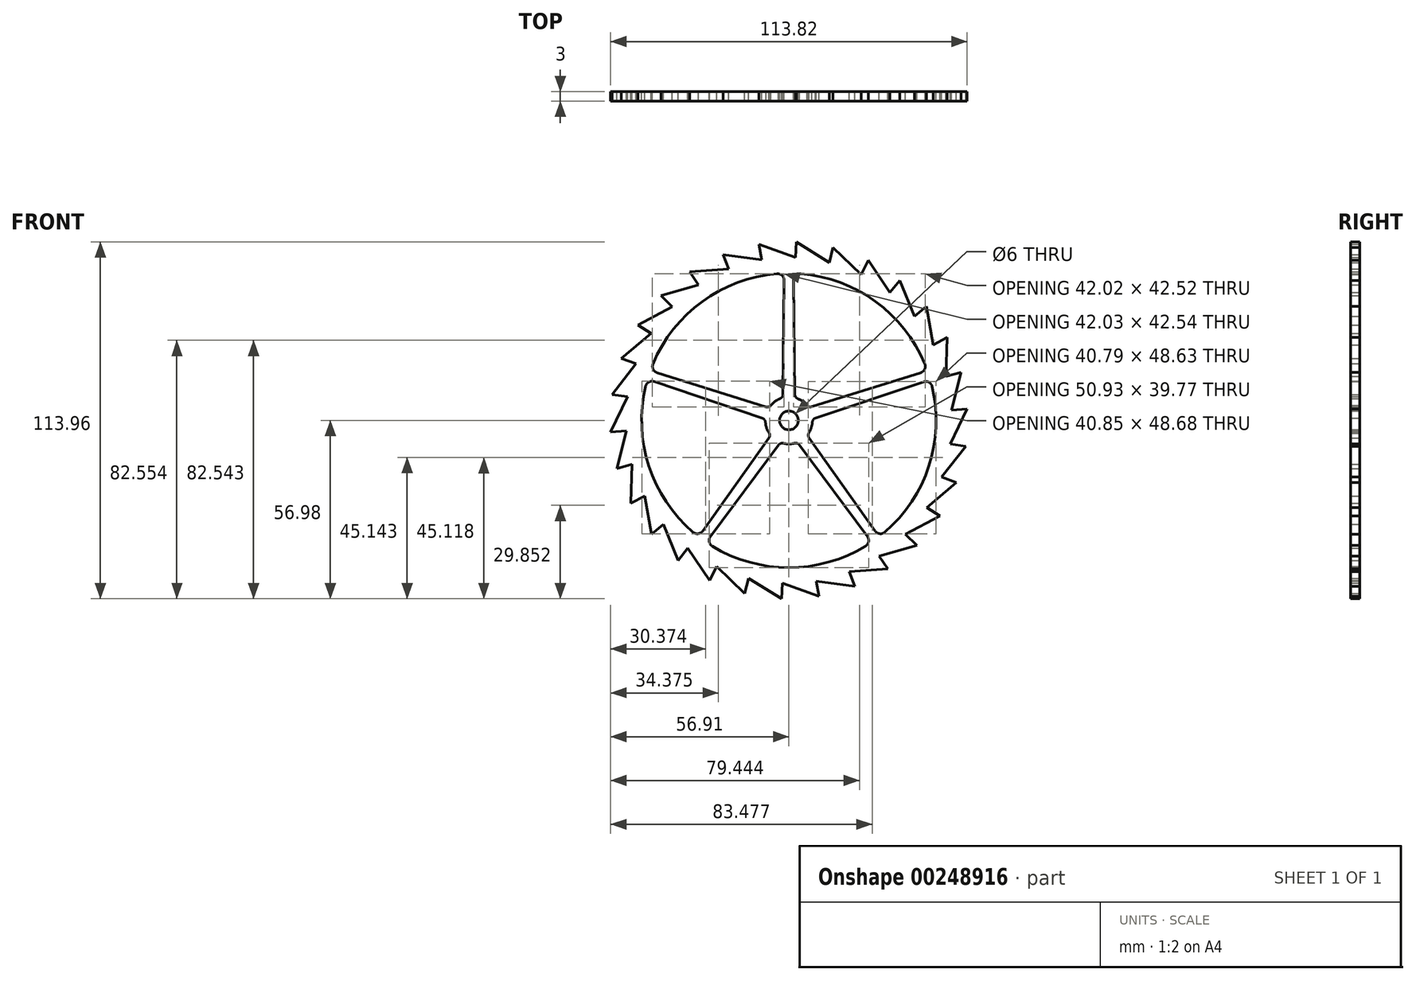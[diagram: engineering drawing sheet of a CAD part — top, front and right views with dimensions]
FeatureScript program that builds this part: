
annotation { "Feature Type Name" : "Feature", "Feature Type Description" : "" }
export const myFeature = defineFeature(function(context is Context, id is Id, definition is map)
    precondition{}
    {
        {
            var Q0;
            Q0=qCreatedBy(makeId("Front.planeOp"),FACE);
            var sketch = newSketch(context, id + "F0", { "sketchPlane" : qUnion([Q0])});
            skLineSegment(sketch, "E0", {"start": v(16.93, -54.43) * mm, "end": v(16.97, -54.42) * mm});
            skCircle(sketch, "E1", {"center": v(-0.03, 0) * mm, "radius": 52 * mm});
            skLineSegment(sketch, "E2.10.0", {"start": v(-40.04, -33.2) * mm, "end": v(-43.9, -36.4) * mm});
            skLineSegment(sketch, "E2.10.1", {"start": v(-43.9, -36.4) * mm, "end": v(-46.08, -24.16) * mm});
            skPoint(sketch, "E3.visualSharp", {"position": v(33.26, -42.81) * mm});
            skArc(sketch, "E3.filletArc", {"start": v(33.31, -42.89) * mm, "mid": v(33.25, -42.83) * mm, "end": v(33.17, -42.8) * mm});
            skArc(sketch, "E4", {"start": v(35.3, 44.72) * mm, "mid": v(35.3, 44.73) * mm, "end": v(35.3, 44.73) * mm});
            skLineSegment(sketch, "E5", {"start": v(32.2, 40.8) * mm, "end": v(32.2, 40.82) * mm});
            skLineSegment(sketch, "E6", {"start": v(0, 52) * mm, "end": v(0, 52.7) * mm, "construction": true});
            skPoint(sketch, "E7.orphan", {"position": v(0, 4.97) * mm});
            skArc(sketch, "E8", {"start": v(-45.72, 10.9) * mm, "mid": v(-44.7, -14.51) * mm, "end": v(-30.6, -35.68) * mm});
            skArc(sketch, "E9", {"start": v(5.77, 4.78) * mm, "mid": v(4.43, 6.04) * mm, "end": v(2.81, 6.94) * mm});
            skLineSegment(sketch, "E10", {"start": v(0, -0.01) * mm, "end": v(0, 64.97) * mm, "construction": true});
            skLineSegment(sketch, "E11", {"start": v(-1.52, 44.7) * mm, "end": v(-1.9, 8.35) * mm});
            skLineSegment(sketch, "E12.MirrorCS", {"start": v(1.52, 44.84) * mm, "end": v(1.9, 8.29) * mm});
            skLineSegment(sketch, "E13.1.0", {"start": v(-44.26, 15.93) * mm, "end": v(-44.22, 15.92) * mm});
            skLineSegment(sketch, "E13.1.1", {"start": v(-45.2, 13.14) * mm, "end": v(-45.13, 13.12) * mm});
            skLineSegment(sketch, "E13.2.0", {"start": v(-28.85, -37.17) * mm, "end": v(-28.83, -37.13) * mm});
            skLineSegment(sketch, "E13.2.1", {"start": v(-26.43, -38.93) * mm, "end": v(-26.4, -38.9) * mm});
            skLineSegment(sketch, "E14.2.3.0", {"start": v(26.43, -38.94) * mm, "end": v(26.4, -38.9) * mm});
            skLineSegment(sketch, "E14.3.3.0", {"start": v(28.86, -37.19) * mm, "end": v(28.82, -37.13) * mm});
            skLineSegment(sketch, "E14.2.4.0", {"start": v(45.18, 13.08) * mm, "end": v(45.14, 13.07) * mm});
            skLineSegment(sketch, "E14.3.4.0", {"start": v(42.07, 15.25) * mm, "end": v(7.32, 4.38) * mm});
            skLineSegment(sketch, "E15.trimOffspring", {"start": v(-7.5, 0) * mm, "end": v(-64.05, 0) * mm, "construction": true});
            skArc(sketch, "E16.trimOffspring", {"start": v(-2.87, 6.92) * mm, "mid": v(-4.45, 6.03) * mm, "end": v(-5.77, 4.78) * mm});
            skArc(sketch, "E17.trimOffspring", {"start": v(-7.48, -0.6) * mm, "mid": v(-7.1, -2.42) * mm, "end": v(-6.3, -4.09) * mm});
            skArc(sketch, "E18.trimOffspring", {"start": v(-1.74, -7.3) * mm, "mid": v(0.1, -7.51) * mm, "end": v(1.93, -7.26) * mm});
            skArc(sketch, "E19.trimOffspring", {"start": v(6.33, -4.03) * mm, "mid": v(7.12, -2.37) * mm, "end": v(7.48, -0.58) * mm});
            skArc(sketch, "E20.trimOffspring", {"start": v(43.38, 18.07) * mm, "mid": v(27.62, 38.02) * mm, "end": v(3.77, 46.84) * mm});
            skArc(sketch, "E21.trimOffspring", {"start": v(-3.82, 46.83) * mm, "mid": v(-27.64, 38) * mm, "end": v(-43.39, 18.06) * mm});
            skArc(sketch, "E22.trimOffspring", {"start": v(-24.44, -40.15) * mm, "mid": v(0, -47.01) * mm, "end": v(24.44, -40.15) * mm});
            skArc(sketch, "E23.trimOffspring", {"start": v(30.6, -35.68) * mm, "mid": v(44.7, -14.54) * mm, "end": v(45.73, 10.85) * mm});
            skArc(sketch, "E24", {"start": v(-30.6, -35.68) * mm, "mid": v(-28.98, -36.17) * mm, "end": v(-27.52, -35.3) * mm});
            skArc(sketch, "E25.MirrorC", {"start": v(-24.44, -40.15) * mm, "mid": v(-25.42, -38.75) * mm, "end": v(-25.04, -37.07) * mm});
            skArc(sketch, "E26.MirrorC", {"start": v(24.44, -40.15) * mm, "mid": v(25.42, -38.75) * mm, "end": v(25.05, -37.08) * mm});
            skArc(sketch, "E27.MirrorC", {"start": v(30.6, -35.68) * mm, "mid": v(28.98, -36.17) * mm, "end": v(27.52, -35.3) * mm});
            skArc(sketch, "E28.MirrorC", {"start": v(45.73, 10.85) * mm, "mid": v(44.7, 12.2) * mm, "end": v(43.01, 12.35) * mm});
            skArc(sketch, "E29.MirrorC", {"start": v(43.38, 18.07) * mm, "mid": v(43.35, 16.37) * mm, "end": v(42.07, 15.25) * mm});
            skPoint(sketch, "E30.endSnap0", {"position": v(22.9, 31.47) * mm});
            skArc(sketch, "E31.MirrorC", {"start": v(3.81, 46.83) * mm, "mid": v(2.15, 46.24) * mm, "end": v(1.52, 44.6) * mm});
            skArc(sketch, "E32.MirrorC", {"start": v(-3.82, 46.83) * mm, "mid": v(-2.2, 46.27) * mm, "end": v(-1.52, 44.7) * mm});
            skArc(sketch, "E33.MirrorC", {"start": v(-43.39, 18.06) * mm, "mid": v(-43.35, 16.36) * mm, "end": v(-42.07, 15.24) * mm});
            skArc(sketch, "E34.MirrorC", {"start": v(-45.72, 10.9) * mm, "mid": v(-44.69, 12.25) * mm, "end": v(-43, 12.4) * mm});
            skPoint(sketch, "E35.orphan", {"position": v(1.5, 47.02) * mm});
            skPoint(sketch, "E36.orphan", {"position": v(-1.5, 47.02) * mm});
            skLineSegment(sketch, "E37.trimOffspring", {"start": v(43.01, 12.35) * mm, "end": v(8.5, 0.77) * mm});
            skLineSegment(sketch, "E38.trimOffspring", {"start": v(27.52, -35.3) * mm, "end": v(6.45, -5.62) * mm});
            skLineSegment(sketch, "E39.trimOffspring", {"start": v(25.05, -37.08) * mm, "end": v(3.36, -7.84) * mm});
            skLineSegment(sketch, "E40.trimOffspring", {"start": v(-25.04, -37.07) * mm, "end": v(-3.31, -7.84) * mm});
            skLineSegment(sketch, "E41.trimOffspring", {"start": v(-27.52, -35.3) * mm, "end": v(-6.42, -5.65) * mm});
            skLineSegment(sketch, "E42.trimOffspring", {"start": v(-42.07, 15.24) * mm, "end": v(-7.33, 4.35) * mm});
            skLineSegment(sketch, "E43.trimOffspring", {"start": v(-43, 12.4) * mm, "end": v(-8.54, 0.75) * mm});
            skArc(sketch, "E44", {"start": v(-7.48, -0.6) * mm, "mid": v(-7.8, 0.23) * mm, "end": v(-8.54, 0.75) * mm});
            skArc(sketch, "E45.MirrorCS", {"start": v(2.81, 6.94) * mm, "mid": v(2.17, 7.49) * mm, "end": v(1.9, 8.29) * mm});
            skArc(sketch, "E46.MirrorCS", {"start": v(-1.74, -7.3) * mm, "mid": v(-2.6, -7.35) * mm, "end": v(-3.31, -7.84) * mm});
            skArc(sketch, "E47.MirrorCS", {"start": v(-5.77, 4.78) * mm, "mid": v(-6.49, 4.35) * mm, "end": v(-7.33, 4.35) * mm});
            skArc(sketch, "E48.MirrorCS", {"start": v(-2.87, 6.92) * mm, "mid": v(-2.17, 7.49) * mm, "end": v(-1.9, 8.35) * mm});
            skArc(sketch, "E49.MirrorCS", {"start": v(5.77, 4.78) * mm, "mid": v(6.5, 4.36) * mm, "end": v(7.32, 4.38) * mm});
            skArc(sketch, "E50.MirrorCS", {"start": v(7.48, -0.58) * mm, "mid": v(7.8, 0.24) * mm, "end": v(8.5, 0.77) * mm});
            skArc(sketch, "E51.MirrorCS", {"start": v(6.33, -4.03) * mm, "mid": v(6.17, -4.84) * mm, "end": v(6.45, -5.62) * mm});
            skArc(sketch, "E52.MirrorCS", {"start": v(1.93, -7.26) * mm, "mid": v(2.72, -7.36) * mm, "end": v(3.36, -7.84) * mm});
            skArc(sketch, "E53.trimOffspring", {"start": v(-6.3, -4.09) * mm, "mid": v(-6.11, -4.89) * mm, "end": v(-6.42, -5.65) * mm});
            skCircle(sketch, "E54", {"center": v(0, 0) * mm, "radius": 3 * mm});
            skCircle(sketch, "E55", {"center": v(0, 0) * mm, "radius": 7.32 * mm, "construction": true});
            skLineSegment(sketch, "E56", {"start": v(0, 0) * mm, "end": v(-46.08, -24.16) * mm, "construction": true});
            skLineSegment(sketch, "E57", {"start": v(0, 0) * mm, "end": v(-40.04, -33.2) * mm, "construction": true});
            skLineSegment(sketch, "E58.1.0", {"start": v(-35.36, -44.73) * mm, "end": v(-40.05, -33.21) * mm});
            skLineSegment(sketch, "E58.1.1", {"start": v(-32.26, -40.8) * mm, "end": v(-35.36, -44.73) * mm});
            skLineSegment(sketch, "E58.2.0", {"start": v(-25.3, -51.1) * mm, "end": v(-32.27, -40.81) * mm});
            skLineSegment(sketch, "E58.2.1", {"start": v(-23.08, -46.63) * mm, "end": v(-25.3, -51.1) * mm});
            skLineSegment(sketch, "E58.3.0", {"start": v(-14.11, -55.25) * mm, "end": v(-23.08, -46.63) * mm});
            skLineSegment(sketch, "E58.3.1", {"start": v(-12.88, -50.4) * mm, "end": v(-14.11, -55.25) * mm});
            skLineSegment(sketch, "E58.4.0", {"start": v(-2.32, -56.98) * mm, "end": v(-12.88, -50.4) * mm});
            skLineSegment(sketch, "E58.4.1", {"start": v(-2.12, -51.98) * mm, "end": v(-2.32, -56.98) * mm});
            skLineSegment(sketch, "E58.5.0", {"start": v(9.58, -56.21) * mm, "end": v(-2.12, -51.98) * mm});
            skLineSegment(sketch, "E58.5.1", {"start": v(8.74, -51.28) * mm, "end": v(9.58, -56.21) * mm});
            skLineSegment(sketch, "E58.6.0", {"start": v(21.06, -53) * mm, "end": v(8.74, -51.29) * mm});
            skLineSegment(sketch, "E58.6.1", {"start": v(19.2, -48.35) * mm, "end": v(21.06, -53) * mm});
            skLineSegment(sketch, "E58.7.0", {"start": v(31.61, -47.46) * mm, "end": v(19.21, -48.35) * mm});
            skLineSegment(sketch, "E58.7.1", {"start": v(28.84, -43.3) * mm, "end": v(31.61, -47.46) * mm});
            skLineSegment(sketch, "E58.8.0", {"start": v(40.8, -39.85) * mm, "end": v(28.84, -43.3) * mm});
            skLineSegment(sketch, "E58.8.1", {"start": v(37.21, -36.35) * mm, "end": v(40.8, -39.85) * mm});
            skLineSegment(sketch, "E58.9.0", {"start": v(48.18, -30.5) * mm, "end": v(37.22, -36.36) * mm});
            skLineSegment(sketch, "E58.9.1", {"start": v(43.96, -27.82) * mm, "end": v(48.18, -30.5) * mm});
            skLineSegment(sketch, "E58.10.0", {"start": v(53.47, -19.81) * mm, "end": v(43.96, -27.82) * mm});
            skLineSegment(sketch, "E58.10.1", {"start": v(48.78, -18.08) * mm, "end": v(53.47, -19.81) * mm});
            skLineSegment(sketch, "E58.11.0", {"start": v(56.42, -8.26) * mm, "end": v(48.79, -18.08) * mm});
            skLineSegment(sketch, "E58.11.1", {"start": v(51.47, -7.54) * mm, "end": v(56.42, -8.26) * mm});
            skLineSegment(sketch, "E58.12.0", {"start": v(56.9, 3.65) * mm, "end": v(51.48, -7.54) * mm});
            skLineSegment(sketch, "E58.12.1", {"start": v(51.92, 3.33) * mm, "end": v(56.9, 3.65) * mm});
            skLineSegment(sketch, "E58.13.0", {"start": v(54.9, 15.4) * mm, "end": v(51.92, 3.33) * mm});
            skLineSegment(sketch, "E58.13.1", {"start": v(50.09, 14.05) * mm, "end": v(54.9, 15.4) * mm});
            skLineSegment(sketch, "E58.14.0", {"start": v(50.5, 26.48) * mm, "end": v(50.1, 14.05) * mm});
            skLineSegment(sketch, "E58.14.1", {"start": v(46.07, 24.16) * mm, "end": v(50.5, 26.48) * mm});
            skLineSegment(sketch, "E58.15.0", {"start": v(43.9, 36.4) * mm, "end": v(46.08, 24.16) * mm});
            skLineSegment(sketch, "E58.15.1", {"start": v(40.04, 33.2) * mm, "end": v(43.9, 36.4) * mm});
            skLineSegment(sketch, "E58.16.0", {"start": v(35.36, 44.73) * mm, "end": v(40.05, 33.21) * mm});
            skLineSegment(sketch, "E58.16.1", {"start": v(32.26, 40.8) * mm, "end": v(35.36, 44.73) * mm});
            skLineSegment(sketch, "E58.17.0", {"start": v(25.3, 51.1) * mm, "end": v(32.27, 40.81) * mm});
            skLineSegment(sketch, "E58.17.1", {"start": v(23.08, 46.63) * mm, "end": v(25.3, 51.1) * mm});
            skLineSegment(sketch, "E58.18.0", {"start": v(14.11, 55.25) * mm, "end": v(23.08, 46.63) * mm});
            skLineSegment(sketch, "E58.18.1", {"start": v(12.88, 50.4) * mm, "end": v(14.11, 55.25) * mm});
            skLineSegment(sketch, "E58.19.0", {"start": v(2.32, 56.98) * mm, "end": v(12.88, 50.4) * mm});
            skLineSegment(sketch, "E58.19.1", {"start": v(2.12, 51.98) * mm, "end": v(2.32, 56.98) * mm});
            skLineSegment(sketch, "E58.20.0", {"start": v(-9.58, 56.21) * mm, "end": v(2.12, 51.98) * mm});
            skLineSegment(sketch, "E58.20.1", {"start": v(-8.74, 51.28) * mm, "end": v(-9.58, 56.21) * mm});
            skLineSegment(sketch, "E58.21.0", {"start": v(-21.06, 53) * mm, "end": v(-8.74, 51.29) * mm});
            skLineSegment(sketch, "E58.21.1", {"start": v(-19.2, 48.35) * mm, "end": v(-21.06, 53) * mm});
            skLineSegment(sketch, "E58.22.0", {"start": v(-31.61, 47.46) * mm, "end": v(-19.21, 48.35) * mm});
            skLineSegment(sketch, "E58.22.1", {"start": v(-28.84, 43.3) * mm, "end": v(-31.61, 47.46) * mm});
            skLineSegment(sketch, "E58.23.0", {"start": v(-40.8, 39.85) * mm, "end": v(-28.84, 43.3) * mm});
            skLineSegment(sketch, "E58.23.1", {"start": v(-37.21, 36.35) * mm, "end": v(-40.8, 39.85) * mm});
            skLineSegment(sketch, "E58.24.0", {"start": v(-48.18, 30.5) * mm, "end": v(-37.22, 36.36) * mm});
            skLineSegment(sketch, "E58.24.1", {"start": v(-43.96, 27.82) * mm, "end": v(-48.18, 30.5) * mm});
            skLineSegment(sketch, "E58.25.0", {"start": v(-53.47, 19.81) * mm, "end": v(-43.96, 27.82) * mm});
            skLineSegment(sketch, "E58.25.1", {"start": v(-48.78, 18.08) * mm, "end": v(-53.47, 19.81) * mm});
            skLineSegment(sketch, "E58.26.0", {"start": v(-56.42, 8.26) * mm, "end": v(-48.79, 18.08) * mm});
            skLineSegment(sketch, "E58.26.1", {"start": v(-51.47, 7.54) * mm, "end": v(-56.42, 8.26) * mm});
            skLineSegment(sketch, "E58.27.0", {"start": v(-56.9, -3.65) * mm, "end": v(-51.48, 7.54) * mm});
            skLineSegment(sketch, "E58.27.1", {"start": v(-51.92, -3.33) * mm, "end": v(-56.9, -3.65) * mm});
            skLineSegment(sketch, "E58.28.0", {"start": v(-54.9, -15.4) * mm, "end": v(-51.92, -3.33) * mm});
            skLineSegment(sketch, "E58.28.1", {"start": v(-50.09, -14.05) * mm, "end": v(-54.9, -15.4) * mm});
            skLineSegment(sketch, "E58.29.0", {"start": v(-50.5, -26.48) * mm, "end": v(-50.1, -14.05) * mm});
            skLineSegment(sketch, "E58.29.1", {"start": v(-46.07, -24.16) * mm, "end": v(-50.5, -26.48) * mm});
            skSolve(sketch);
        }
        {
            var Q0;
            {var subQ0=sQuery(id+"F0.wireOp",EDGE,"E58.28.0");var subQ1=sQuery(id+"F0.wireOp",EDGE,"E1");var subQ2=makeQuery(id+"F0.imprint","INTERSECT",VERTEX,{"derivedFrom":[subQ1,subQ0]});Q0=makeQuery(id+"F0.imprint","IMPRINT",FACE,{"disambiguationData":[TD([[makeQuery(id+"F0.imprint","IMPRINT",EDGE,{"disambiguationData":[TD([[subQ2,-1.0]])],"derivedFrom":subQ1}),-1.0]])]});}
            var Q1;
            {var subQ0=sQuery(id+"F0.wireOp",EDGE,"E58.29.0");var subQ1=sQuery(id+"F0.wireOp",EDGE,"E1");var subQ2=makeQuery(id+"F0.imprint","INTERSECT",VERTEX,{"derivedFrom":[subQ1,subQ0]});Q1=makeQuery(id+"F0.imprint","IMPRINT",FACE,{"disambiguationData":[TD([[makeQuery(id+"F0.imprint","IMPRINT",EDGE,{"disambiguationData":[TD([[subQ2,-1.0]])],"derivedFrom":subQ1}),-1.0]])]});}
            var Q2;
            {var subQ0=sQuery(id+"F0.wireOp",EDGE,"E2.10.1");var subQ1=sQuery(id+"F0.wireOp",EDGE,"E1");var subQ2=makeQuery(id+"F0.imprint","INTERSECT",VERTEX,{"derivedFrom":[subQ1,subQ0]});Q2=makeQuery(id+"F0.imprint","IMPRINT",FACE,{"disambiguationData":[TD([[makeQuery(id+"F0.imprint","IMPRINT",EDGE,{"disambiguationData":[TD([[subQ2,-1.0]])],"derivedFrom":subQ1}),-1.0]])]});}
            var Q3;
            {var subQ34=sQuery(id+"F0.wireOp",EDGE,"E58.1.0");Q3=makeQuery(id+"F0.imprint","IMPRINT",FACE,{"disambiguationData":[TD([[makeQuery(id+"F0.imprint","IMPRINT",EDGE,{"derivedFrom":subQ34}),-1.0]])]});}
            var Q4;
            {var subQ0=sQuery(id+"F0.wireOp",EDGE,"E58.27.0");var subQ1=sQuery(id+"F0.wireOp",EDGE,"E1");var subQ2=makeQuery(id+"F0.imprint","INTERSECT",VERTEX,{"derivedFrom":[subQ1,subQ0]});Q4=makeQuery(id+"F0.imprint","IMPRINT",FACE,{"disambiguationData":[TD([[makeQuery(id+"F0.imprint","IMPRINT",EDGE,{"disambiguationData":[TD([[subQ2,-1.0]])],"derivedFrom":subQ1}),-1.0]])]});}
            var Q5;
            {var subQ0=sQuery(id+"F0.wireOp",EDGE,"E58.26.0");var subQ1=sQuery(id+"F0.wireOp",EDGE,"E1");var subQ2=makeQuery(id+"F0.imprint","INTERSECT",VERTEX,{"derivedFrom":[subQ1,subQ0]});Q5=makeQuery(id+"F0.imprint","IMPRINT",FACE,{"disambiguationData":[TD([[makeQuery(id+"F0.imprint","IMPRINT",EDGE,{"disambiguationData":[TD([[subQ2,-1.0]])],"derivedFrom":subQ1}),-1.0]])]});}
            var Q6;
            {var subQ0=sQuery(id+"F0.wireOp",EDGE,"E58.25.0");var subQ1=sQuery(id+"F0.wireOp",EDGE,"E1");var subQ2=makeQuery(id+"F0.imprint","INTERSECT",VERTEX,{"derivedFrom":[subQ1,subQ0]});Q6=makeQuery(id+"F0.imprint","IMPRINT",FACE,{"disambiguationData":[TD([[makeQuery(id+"F0.imprint","IMPRINT",EDGE,{"disambiguationData":[TD([[subQ2,-1.0]])],"derivedFrom":subQ1}),-1.0]])]});}
            var Q7;
            {var subQ5=sQuery(id+"F0.wireOp",EDGE,"E58.24.0");Q7=makeQuery(id+"F0.imprint","IMPRINT",FACE,{"disambiguationData":[TD([[makeQuery(id+"F0.imprint","IMPRINT",EDGE,{"derivedFrom":subQ5}),-1.0]])]});}
            var Q8;
            Q8=makeQuery(id+"F0.imprint","IMPRINT",FACE,{"disambiguationData":[TD([[makeQuery(id+"F0.imprint","IMPRINT",EDGE,{"derivedFrom":sQuery(id+"F0.wireOp",EDGE,"E8")}),-1.0]])]});
            extrude(context, id + "F1", {"entities" : qUnion([Q0, Q1, Q2, Q3, Q4, Q5, Q6, Q7, Q8]), "depth" : 3 * mm});
        }
    });
